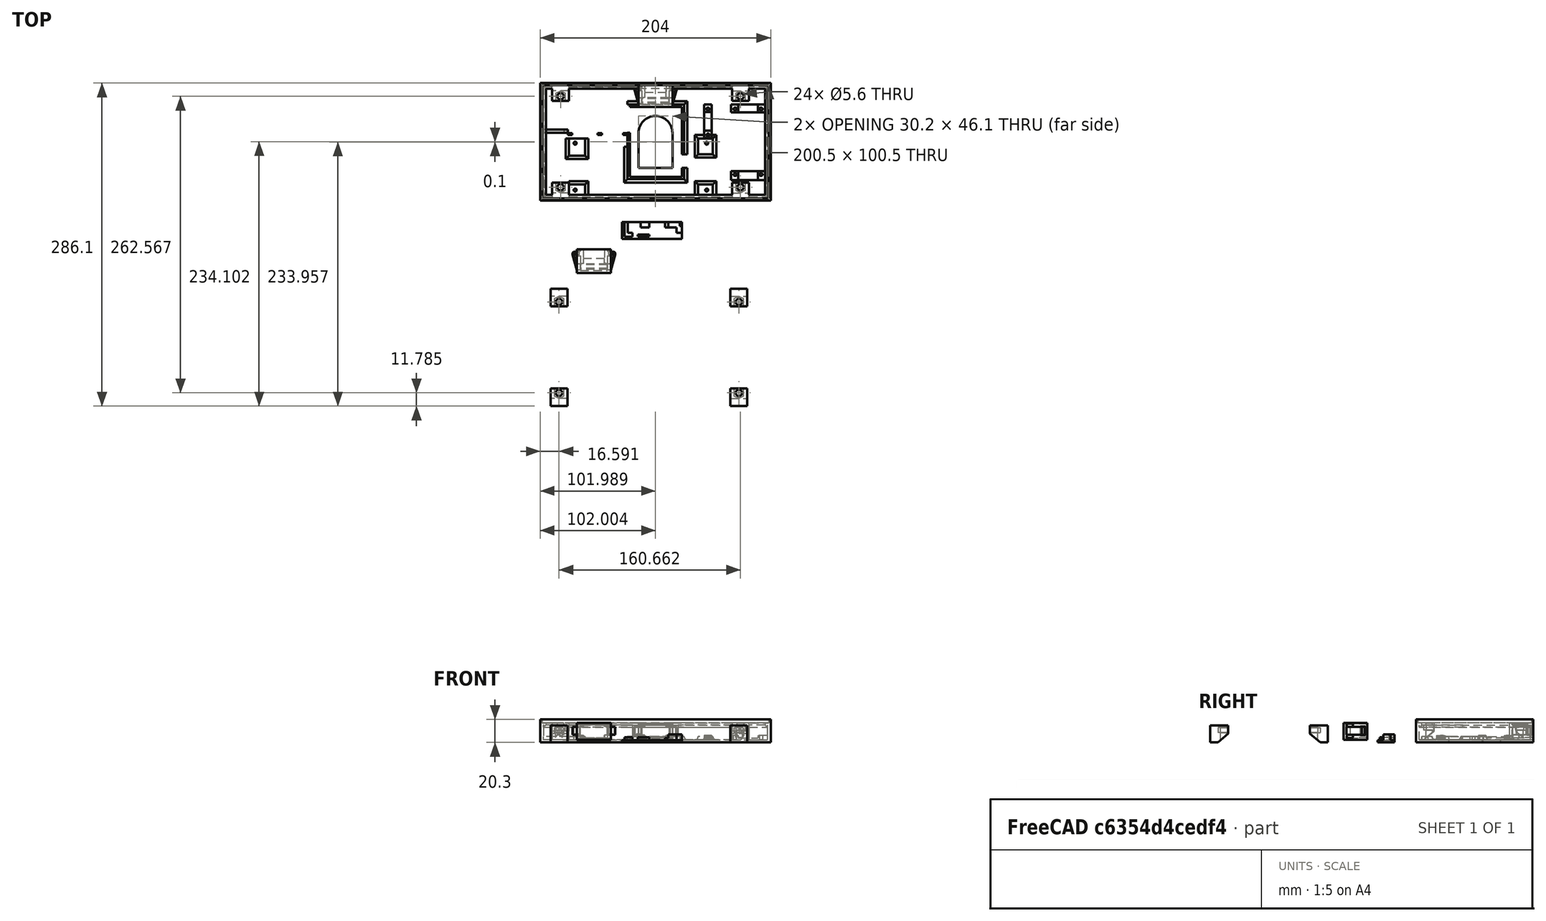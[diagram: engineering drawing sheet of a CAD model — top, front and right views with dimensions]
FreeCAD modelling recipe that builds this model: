
FCSTD DOCUMENT  (FreeCAD 0.18.4R)
Label: lamp.base.new
License: All rights reserved
LicenseURL: http://en.wikipedia.org/wiki/All_rights_reserved
objects: Part::Extrusion×98, Part::Feature×63, Part::Part2DObjectPython×54, Part::Cut×37, Part::MultiFuse×32, Part::MultiCommon×11, Part::Fuse×1
note: 296 computed .brp shape members not serialized (recipe doc carries the construction recipe); baked Part::Feature solids carry a one-line shape summary decoded from their .brp

FEATURE [Part::Feature] Fusion004001_solid  label="Power Connector Box-Hiddem"
  Placement = pos=(186.233,-140.75,0) rot=(0,0,1;0rad)
  shape: bbox 38 x 21 x 15 mm, 84 faces (baked)
FEATURE [Part::Feature] Fusion076089004005010001  label="RaspberryPi supplier"
  shape: bbox 32.15 x 67 x 4 mm, 24 faces, 2 solids (baked)
FEATURE [Part::Feature] Fusion076089004005008002002002002003004002009002004002005004002001  label="Power supply box cap - Hidden"
  shape: bbox 53 x 15.1 x 7 mm, 39 faces (baked)
FEATURE [Part::Part2DObjectPython] Rectangle007  # Draft 2D object (typed FeaturePython)
  ChamferSize = 0
  Columns = 1
  FilletRadius = 0
  Height = 1.8
  Length = 3.8
  MakeFace = true
  Placement = pos=(43.1036,-626.313,9.00025) rot=(1,0,0;3.14159rad)
  Rows = 1
FEATURE [Part::Part2DObjectPython] Rectangle008  # Draft 2D object (typed FeaturePython)
  ChamferSize = 0
  Columns = 1
  FilletRadius = 0
  Height = 1.8
  Length = 3.8
  MakeFace = true
  Placement = pos=(92.1036,-626.313,9.00025) rot=(1,0,0;3.14159rad)
  Rows = 1
FEATURE [Part::Part2DObjectPython] Rectangle009  # Draft 2D object (typed FeaturePython)
  ChamferSize = 0
  Columns = 1
  FilletRadius = 0
  Height = 1.8
  Length = 3.8
  MakeFace = true
  Placement = pos=(69.6036,-626.313,9.00025) rot=(1,0,0;3.14159rad)
  Rows = 1
FEATURE [Part::Extrusion] Extrusion037
  Base = -> Rectangle008
  Dir = (-1.26165e-08,1.08079e-10,-0.3)
  DirMode = 0
  FaceMakerClass = Part::FaceMakerBullseye
  LengthFwd = 0
  LengthRev = 0
  Solid = true
  Symmetric = false
FEATURE [Part::Extrusion] Extrusion038
  Base = -> Rectangle009
  Dir = (-1.26164e-08,1.08078e-10,-0.299999)
  DirMode = 0
  FaceMakerClass = Part::FaceMakerBullseye
  LengthFwd = 0
  LengthRev = 0
  Solid = true
  Symmetric = false
FEATURE [Part::Extrusion] Extrusion039
  Base = -> Rectangle007
  Dir = (-1.26164e-08,1.08078e-10,-0.299998)
  DirMode = 0
  FaceMakerClass = Part::FaceMakerBullseye
  LengthFwd = 0
  LengthRev = 0
  Solid = true
  Symmetric = false
FEATURE [Part::Part2DObjectPython] Rectangle010  # Draft 2D object (typed FeaturePython)
  ChamferSize = 0
  Columns = 1
  FilletRadius = 0
  Height = 3
  Length = 3
  MakeFace = true
  Placement = pos=(149.004,-645.218,12.0003) rot=(0,0.707107,-0.707107;3.14159rad)
  Rows = 1
FEATURE [Part::Part2DObjectPython] Circle002  # Draft 2D object (typed FeaturePython)
  FirstAngle = 0
  LastAngle = 0
  MakeFace = true
  Placement = pos=(149.004,-645.218,12.0003) rot=(0,0.707107,-0.707107;3.14159rad)
  Radius = 3
FEATURE [Part::Extrusion] Extrusion040
  Base = -> Rectangle010
  Dir = (-7e-16,47.0048,1.04e-14)
  DirMode = 0
  FaceMakerClass = Part::FaceMakerBullseye
  LengthFwd = 0
  LengthRev = 0
  Solid = true
  Symmetric = false
FEATURE [Part::Extrusion] Extrusion041
  Base = -> Circle002
  Dir = (-7e-16,47.0048,1.04e-14)
  DirMode = 0
  FaceMakerClass = Part::FaceMakerBullseye
  LengthFwd = 0
  LengthRev = 0
  Solid = true
  Symmetric = false
FEATURE [Part::Cut] Cut279012006003005
  Base = -> Extrusion040
  Tool = -> Extrusion041
FEATURE [Part::Part2DObjectPython] Rectangle011  # Draft 2D object (typed FeaturePython)
  ChamferSize = 0
  Columns = 1
  FilletRadius = 0
  Height = 3
  Length = 3
  MakeFace = true
  Placement = pos=(146.004,-667.213,9.00025) rot=(0.57735,-0.57735,-0.57735;2.0944rad)
  Rows = 1
FEATURE [Part::Part2DObjectPython] Circle003  # Draft 2D object (typed FeaturePython)
  FirstAngle = 0
  LastAngle = 0
  MakeFace = true
  Placement = pos=(146.004,-670.213,12.0003) rot=(0.57735,-0.57735,-0.57735;2.0944rad)
  Radius = 3
FEATURE [Part::Extrusion] Extrusion044
  Base = -> Rectangle011
  Dir = (-52.9386,1.18e-14,5.9e-15)
  DirMode = 0
  FaceMakerClass = Part::FaceMakerBullseye
  LengthFwd = 0
  LengthRev = 0
  Solid = true
  Symmetric = false
FEATURE [Part::Extrusion] Extrusion045
  Base = -> Circle003
  Dir = (-52.9386,1.18e-14,5.9e-15)
  DirMode = 0
  FaceMakerClass = Part::FaceMakerBullseye
  LengthFwd = 0
  LengthRev = 0
  Solid = true
  Symmetric = false
FEATURE [Part::Cut] Cut279012006003006
  Base = -> Extrusion044
  Tool = -> Extrusion045
FEATURE [Part::Feature] Face020
  shape: bbox 2e-07 x 3 x 3 mm, 1 faces, 0 solids (baked)
FEATURE [Part::Extrusion] Extrusion046
  Base = -> Face020
  Dir = (3,-7e-16,-3e-16)
  DirMode = 0
  FaceMakerClass = Part::FaceMakerBullseye
  LengthFwd = 0
  LengthRev = 0
  Solid = true
  Symmetric = false
FEATURE [Part::Part2DObjectPython] Circle004  # Draft 2D object (typed FeaturePython)
  FirstAngle = 0
  LastAngle = 0
  MakeFace = true
  Placement = pos=(149.004,-657.213,12.0003) rot=(-1,0,0;1.5708rad)
  Radius = 3
FEATURE [Part::Feature] Face021
  Placement = pos=(0,-11.9952,-3e-15) rot=(0,0,1;0rad)
  shape: bbox 3 x 2e-07 x 3 mm, 1 faces, 0 solids (baked)
FEATURE [Part::Extrusion] Extrusion047
  Base = -> Face021
  Dir = (2e-16,-13,-2.9e-15)
  DirMode = 0
  FaceMakerClass = Part::FaceMakerBullseye
  LengthFwd = 0
  LengthRev = 0
  Solid = true
  Symmetric = false
FEATURE [Part::Extrusion] Extrusion048
  Base = -> Circle004
  Dir = (-2e-16,-13,-2.9e-15)
  DirMode = 0
  FaceMakerClass = Part::FaceMakerBullseye
  LengthFwd = 0
  LengthRev = 0
  Solid = true
  Symmetric = false
FEATURE [Part::Cut] Cut279012006003007
  Base = -> Extrusion046
  Tool = -> Extrusion048
FEATURE [Part::Feature] Face023
  Placement = pos=(0,-24.9952,-6e-15) rot=(0,0,1;0rad)
  shape: bbox 3 x 2e-07 x 3 mm, 1 faces, 0 solids (baked)
FEATURE [Part::Extrusion] Extrusion051
  Base = -> Face023
  Dir = (0,3,7e-16)
  DirMode = 0
  FaceMakerClass = Part::FaceMakerBullseye
  LengthFwd = 0
  LengthRev = 0
  Solid = true
  Symmetric = false
FEATURE [Part::Cut] Cut279012006003008
  Base = -> Extrusion047
  Tool = -> Extrusion051
FEATURE [Part::MultiFuse] Fusion076089004005008002002002002003004002009002004002005004002002
  Shapes = -> [Cut279012006003006,Cut279012006003007,Cut279012006003008]
FEATURE [Part::MultiFuse] Fusion076089004005008002002002002003004002009002004002005004002003
  Shapes = -> [Cut279012006003005,Fusion076089004005008002002002002003004002009002004002005004002002]
FEATURE [Part::Feature] Face024
  shape: bbox 2e-07 x 3 x 3 mm, 1 faces, 0 solids (baked)
FEATURE [Part::Extrusion] Extrusion052
  Base = -> Face024
  Dir = (-0.0614462,0,0)
  DirMode = 0
  FaceMakerClass = Part::FaceMakerBullseye
  LengthFwd = 0
  LengthRev = 0
  Solid = true
  Symmetric = false
FEATURE [Part::MultiFuse] Fusion076089004005008002002002002003004002009002004002005004002004
  Shapes = -> [Fusion076089004005008002002002002003004002009002004002005004002003,Extrusion052]
FEATURE [Part::Part2DObjectPython] Rectangle012  # Draft 2D object (typed FeaturePython)
  ChamferSize = 0
  Columns = 1
  FilletRadius = 0
  Height = 3
  Length = 3
  MakeFace = true
  Placement = pos=(96.0036,-667.213,9.00025) rot=(0,0.707107,0.707107;3.14159rad)
  Rows = 1
  Support = -> [Fusion076089004005008002002002002003004002009002004002005004002004]
FEATURE [Part::Extrusion] Extrusion053
  Base = -> Rectangle012
  Dir = (6.9e-15,38.8,8.6e-15)
  DirMode = 0
  FaceMakerClass = Part::FaceMakerBullseye
  LengthFwd = 0
  LengthRev = 0
  Solid = true
  Symmetric = false
FEATURE [Part::Part2DObjectPython] Circle005  # Draft 2D object (typed FeaturePython)
  FirstAngle = 0
  LastAngle = 0
  MakeFace = true
  Placement = pos=(93.0036,-667.213,12.0003) rot=(0,0.707107,0.707107;3.14159rad)
  Radius = 3
  Support = -> [Extrusion053]
FEATURE [Part::Extrusion] Extrusion054
  Base = -> Circle005
  Dir = (6.9e-15,38.8,8.6e-15)
  DirMode = 0
  FaceMakerClass = Part::FaceMakerBullseye
  LengthFwd = 0
  LengthRev = 0
  Solid = true
  Symmetric = false
FEATURE [Part::Cut] Cut279012006003009
  Base = -> Extrusion053
  Tool = -> Extrusion054
FEATURE [Part::Feature] Face025
  shape: bbox 3 x 2e-07 x 3 mm, 1 faces, 0 solids (baked)
FEATURE [Part::Extrusion] Extrusion055
  Base = -> Face025
  Dir = (-5e-16,-2.96852,-7e-16)
  DirMode = 0
  FaceMakerClass = Part::FaceMakerBullseye
  LengthFwd = 0
  LengthRev = 0
  Solid = true
  Symmetric = false
FEATURE [Part::MultiFuse] Fusion076089004005008002002002002003004002009002004002005004002005
  Shapes = -> [Cut279012006003009,Extrusion055]
FEATURE [Part::Feature] Face026
  shape: bbox 3 x 2e-07 x 3 mm, 1 faces, 0 solids (baked)
FEATURE [Part::Extrusion] Extrusion056
  Base = -> Face026
  Dir = (-1.8e-15,-10,-2.2e-15)
  DirMode = 0
  FaceMakerClass = Part::FaceMakerBullseye
  LengthFwd = 0
  LengthRev = 0
  Solid = true
  Symmetric = false
FEATURE [Part::Cut] Cut279012006003010
  Base = -> Fusion076089004005008002002002002003004002009002004002005004002005
  Tool = -> Extrusion056
FEATURE [Part::Feature] Face028
  Placement = pos=(-1e-15,-2.96852,-1e-15) rot=(0,0,1;0rad)
  shape: bbox 3 x 2e-07 x 3 mm, 1 faces, 0 solids (baked)
FEATURE [Part::Extrusion] Extrusion057
  Base = -> Face028
  Dir = (5e-16,2.96852,7e-16)
  DirMode = 0
  FaceMakerClass = Part::FaceMakerBullseye
  LengthFwd = 0
  LengthRev = 0
  Solid = true
  Symmetric = false
FEATURE [Part::Feature] Face029
  Placement = pos=(-0.0614462,0,0) rot=(0,0,1;0rad)
  shape: bbox 2e-07 x 3 x 3 mm, 1 faces, 0 solids (baked)
FEATURE [Part::Extrusion] Extrusion058
  Base = -> Face029
  Dir = (3,-7e-16,-3e-16)
  DirMode = 0
  FaceMakerClass = Part::FaceMakerBullseye
  LengthFwd = 0
  LengthRev = 0
  Solid = true
  Symmetric = false
FEATURE [Part::Cut] Cut279012006003011
  Base = -> Cut279012006003010
  Tool = -> Extrusion057
FEATURE [Part::Cut] Cut279012006003012
  Base = -> Fusion076089004005008002002002002003004002009002004002005004002004
  Tool = -> Extrusion058
FEATURE [Part::Feature] Face030
  Placement = pos=(2.93855,-1e-15,0) rot=(0,0,1;0rad)
  shape: bbox 2e-07 x 3 x 3 mm, 1 faces, 0 solids (baked)
FEATURE [Part::Extrusion] Extrusion059
  Base = -> Face030
  Dir = (-3,7e-16,3e-16)
  DirMode = 0
  FaceMakerClass = Part::FaceMakerBullseye
  LengthFwd = 0
  LengthRev = 0
  Solid = true
  Symmetric = false
FEATURE [Part::Feature] Face031
  shape: bbox 3 x 2e-07 x 3 mm, 1 faces, 0 solids (baked)
FEATURE [Part::Extrusion] Extrusion060
  Base = -> Face031
  Dir = (-5e-16,-3,-7e-16)
  DirMode = 0
  FaceMakerClass = Part::FaceMakerBullseye
  LengthFwd = 0
  LengthRev = 0
  Solid = true
  Symmetric = false
FEATURE [Part::MultiCommon] Common
  Shapes = -> [Extrusion059,Extrusion060]
FEATURE [Part::MultiFuse] Fusion076089004005008002002002002003004002009002004002005004002006
  Shapes = -> [Common,Cut279012006003012,Cut279012006003011]
FEATURE [Part::Part2DObjectPython] Rectangle013  # Draft 2D object (typed FeaturePython)
  ChamferSize = 0
  Columns = 1
  FilletRadius = 0
  Height = 3
  Length = 3
  MakeFace = true
  Placement = pos=(146.004,-601.213,12.0003) rot=(0.57735,0.57735,-0.57735;4.18879rad)
  Rows = 1
  Support = -> [Fusion076089004005008002002002002003004002009002004002005004002006]
FEATURE [Part::Extrusion] Extrusion061
  Base = -> Rectangle013
  Dir = (-10.3,0,-2.3e-15)
  DirMode = 0
  FaceMakerClass = Part::FaceMakerBullseye
  LengthFwd = 0
  LengthRev = 0
  Solid = true
  Symmetric = false
FEATURE [Part::Part2DObjectPython] Circle006  # Draft 2D object (typed FeaturePython)
  FirstAngle = 0
  LastAngle = 0
  MakeFace = true
  Placement = pos=(146.004,-598.213,12.0003) rot=(0.57735,0.57735,-0.57735;4.18879rad)
  Radius = 3
FEATURE [Part::Extrusion] Extrusion062
  Base = -> Circle006
  Dir = (-10.3,0,-2.3e-15)
  DirMode = 0
  FaceMakerClass = Part::FaceMakerBullseye
  LengthFwd = 0
  LengthRev = 0
  Solid = true
  Symmetric = false
FEATURE [Part::Cut] Cut279012006003013
  Base = -> Extrusion061
  Tool = -> Extrusion062
FEATURE [Part::Feature] Face032
  shape: bbox 3 x 2e-07 x 3 mm, 1 faces, 0 solids (baked)
FEATURE [Part::Extrusion] Extrusion063
  Base = -> Face032
  Dir = (0,-3,-7e-16)
  DirMode = 0
  FaceMakerClass = Part::FaceMakerBullseye
  LengthFwd = 0
  LengthRev = 0
  Solid = true
  Symmetric = false
FEATURE [Part::Cut] Cut279012006003014
  Base = -> Fusion076089004005008002002002002003004002009002004002005004002006
  Tool = -> Extrusion063
FEATURE [Part::Feature] Face033
  Placement = pos=(0,-3,-1e-15) rot=(0,0,1;0rad)
  shape: bbox 3 x 2e-07 x 3 mm, 1 faces, 0 solids (baked)
FEATURE [Part::Extrusion] Extrusion064
  Base = -> Face033
  Dir = (0,3,7e-16)
  DirMode = 0
  FaceMakerClass = Part::FaceMakerBullseye
  LengthFwd = 0
  LengthRev = 0
  Solid = true
  Symmetric = false
FEATURE [Part::Feature] Face034
  shape: bbox 2e-07 x 3 x 3 mm, 1 faces, 0 solids (baked)
FEATURE [Part::Extrusion] Extrusion065
  Base = -> Face034
  Dir = (3,0,7e-16)
  DirMode = 0
  FaceMakerClass = Part::FaceMakerBullseye
  LengthFwd = 0
  LengthRev = 0
  Solid = true
  Symmetric = false
FEATURE [Part::MultiCommon] Common001
  Shapes = -> [Extrusion064,Extrusion065]
FEATURE [Part::MultiFuse] Fusion076089004005008002002002002003004002009002004002005004002007
  Shapes = -> [Common001,Cut279012006003013,Cut279012006003014]
FEATURE [Part::Part2DObjectPython] Rectangle014  # Draft 2D object (typed FeaturePython)
  ChamferSize = 0
  Columns = 1
  FilletRadius = 0
  Height = 3
  Length = 3
  MakeFace = true
  Placement = pos=(171.504,-671.954,9) rot=(0.57735,0.57735,0.57735;2.0944rad)
  Rows = 1
FEATURE [Part::Part2DObjectPython] Circle007  # Draft 2D object (typed FeaturePython)
  FirstAngle = 0
  LastAngle = 0
  MakeFace = true
  Placement = pos=(171.504,-668.954,12) rot=(0.57735,0.57735,0.57735;2.0944rad)
  Radius = 3
FEATURE [Part::Extrusion] Extrusion066
  Base = -> Rectangle014
  Dir = (-12.95,0,0)
  DirMode = 0
  FaceMakerClass = Part::FaceMakerBullseye
  LengthFwd = 0
  LengthRev = 0
  Solid = true
  Symmetric = false
FEATURE [Part::Extrusion] Extrusion067
  Base = -> Circle007
  Dir = (-12.95,0,0)
  DirMode = 0
  FaceMakerClass = Part::FaceMakerBullseye
  LengthFwd = 0
  LengthRev = 0
  Solid = true
  Symmetric = false
FEATURE [Part::Cut] Cut279012006003015
  Base = -> Extrusion066
  Tool = -> Extrusion067
FEATURE [Part::Part2DObjectPython] Rectangle015  # Draft 2D object (typed FeaturePython)
  ChamferSize = 0
  Columns = 1
  FilletRadius = 0
  Height = 3
  Length = 3
  MakeFace = true
  Placement = pos=(171.504,-631.118,9) rot=(0.57735,0.57735,0.57735;2.0944rad)
  Rows = 1
FEATURE [Part::Part2DObjectPython] Circle008  # Draft 2D object (typed FeaturePython)
  FirstAngle = 0
  LastAngle = 0
  MakeFace = true
  Placement = pos=(171.504,-628.118,12) rot=(0.57735,0.57735,0.57735;2.0944rad)
  Radius = 3
  Support = -> [Rectangle015]
FEATURE [Part::Extrusion] Extrusion068
  Base = -> Rectangle015
  Dir = (-12.95,0,0)
  DirMode = 0
  FaceMakerClass = Part::FaceMakerBullseye
  LengthFwd = 0
  LengthRev = 0
  Solid = true
  Symmetric = false
FEATURE [Part::Extrusion] Extrusion069
  Base = -> Circle008
  Dir = (-12.95,0,0)
  DirMode = 0
  FaceMakerClass = Part::FaceMakerBullseye
  LengthFwd = 0
  LengthRev = 0
  Solid = true
  Symmetric = false
FEATURE [Part::Cut] Cut279012006003016
  Base = -> Extrusion068
  Tool = -> Extrusion069
FEATURE [Part::Part2DObjectPython] Rectangle016  # Draft 2D object (typed FeaturePython)
  ChamferSize = 0
  Columns = 1
  FilletRadius = 0
  Height = 2.86268
  Length = 2.86268
  MakeFace = true
  Placement = pos=(58.2286,-671.954,9.13732) rot=(0.57735,0.57735,0.57735;2.0944rad)
  Rows = 1
FEATURE [Part::Extrusion] Extrusion070
  Base = -> Rectangle016
  Dir = (-14.025,7.8e-15,7e-15)
  DirMode = 0
  FaceMakerClass = Part::FaceMakerBullseye
  LengthFwd = 0
  LengthRev = 0
  Solid = true
  Symmetric = false
FEATURE [Part::Part2DObjectPython] Circle009  # Draft 2D object (typed FeaturePython)
  FirstAngle = 0
  LastAngle = 0
  MakeFace = true
  Placement = pos=(58.2286,-669.091,12) rot=(0.57735,0.57735,0.57735;2.0944rad)
  Radius = 2.86268
FEATURE [Part::Extrusion] Extrusion071
  Base = -> Circle009
  Dir = (-14.025,7.8e-15,7e-15)
  DirMode = 0
  FaceMakerClass = Part::FaceMakerBullseye
  LengthFwd = 0
  LengthRev = 0
  Solid = true
  Symmetric = false
FEATURE [Part::Cut] Cut279012006003017
  Base = -> Extrusion070
  Tool = -> Extrusion071
FEATURE [Part::Part2DObjectPython] Rectangle017  # Draft 2D object (typed FeaturePython)
  ChamferSize = 0
  Columns = 1
  FilletRadius = 0
  Height = 3
  Length = 3
  MakeFace = true
  Placement = pos=(58.2286,-649.418,9) rot=(0.57735,0.57735,0.57735;2.0944rad)
  Rows = 1
FEATURE [Part::Part2DObjectPython] Circle010  # Draft 2D object (typed FeaturePython)
  FirstAngle = 0
  LastAngle = 0
  MakeFace = true
  Placement = pos=(58.2286,-649.418,12) rot=(0.57735,0.57735,0.57735;2.0944rad)
  Radius = 3
FEATURE [Part::Extrusion] Extrusion072
  Base = -> Rectangle017
  Dir = (-14.025,7.8e-15,7e-15)
  DirMode = 0
  FaceMakerClass = Part::FaceMakerBullseye
  LengthFwd = 0
  LengthRev = 0
  Solid = true
  Symmetric = false
FEATURE [Part::Extrusion] Extrusion073
  Base = -> Circle010
  Dir = (-14.025,7.8e-15,7e-15)
  DirMode = 0
  FaceMakerClass = Part::FaceMakerBullseye
  LengthFwd = 0
  LengthRev = 0
  Solid = true
  Symmetric = false
FEATURE [Part::Cut] Cut279012006003018
  Base = -> Extrusion072
  Tool = -> Extrusion073
FEATURE [Part::Part2DObjectPython] Rectangle018  # Draft 2D object (typed FeaturePython)
  ChamferSize = 0
  Columns = 1
  FilletRadius = 0
  Height = 3
  Length = 3
  MakeFace = true
  Placement = pos=(174.504,-671.954,9) rot=(0,0.707107,0.707107;3.14159rad)
  Rows = 1
FEATURE [Part::Part2DObjectPython] Circle011  # Draft 2D object (typed FeaturePython)
  FirstAngle = 0
  LastAngle = 0
  MakeFace = true
  Placement = pos=(174.504,-671.954,12) rot=(0,0.707107,0.707107;3.14159rad)
  Radius = 3
FEATURE [Part::Extrusion] Extrusion074
  Base = -> Rectangle018
  Dir = (1.3e-15,-9.16419,2e-15)
  DirMode = 0
  FaceMakerClass = Part::FaceMakerBullseye
  LengthFwd = 0
  LengthRev = 0
  Solid = true
  Symmetric = false
FEATURE [Part::Extrusion] Extrusion075
  Base = -> Circle011
  Dir = (1.3e-15,-9.16419,2e-15)
  DirMode = 0
  FaceMakerClass = Part::FaceMakerBullseye
  LengthFwd = 0
  LengthRev = 0
  Solid = true
  Symmetric = false
FEATURE [Part::Cut] Cut279012006003019
  Base = -> Extrusion074
  Tool = -> Extrusion075
FEATURE [Part::Part2DObjectPython] Rectangle019  # Draft 2D object (typed FeaturePython)
  ChamferSize = 0
  Columns = 1
  FilletRadius = 0
  Height = 3
  Length = 3
  MakeFace = true
  Placement = pos=(158.554,-671.954,9) rot=(0,0.707107,0.707107;3.14159rad)
  Rows = 1
FEATURE [Part::Part2DObjectPython] Circle012  # Draft 2D object (typed FeaturePython)
  FirstAngle = 0
  LastAngle = 0
  MakeFace = true
  Placement = pos=(155.554,-671.954,12) rot=(0,0.707107,0.707107;3.14159rad)
  Radius = 3
  Support = -> [Rectangle019]
FEATURE [Part::Extrusion] Extrusion076
  Base = -> Rectangle019
  Dir = (1.3e-15,-9.16419,2e-15)
  DirMode = 0
  FaceMakerClass = Part::FaceMakerBullseye
  LengthFwd = 0
  LengthRev = 0
  Solid = true
  Symmetric = false
FEATURE [Part::Extrusion] Extrusion077
  Base = -> Circle012
  Dir = (1.3e-15,-9.16419,2e-15)
  DirMode = 0
  FaceMakerClass = Part::FaceMakerBullseye
  LengthFwd = 0
  LengthRev = 0
  Solid = true
  Symmetric = false
FEATURE [Part::Cut] Cut279012006003020
  Base = -> Extrusion076
  Tool = -> Extrusion077
FEATURE [Part::Part2DObjectPython] Rectangle020  # Draft 2D object (typed FeaturePython)
  ChamferSize = 0
  Columns = 1
  FilletRadius = 0
  Height = 2.86268
  Length = 3
  MakeFace = true
  Placement = pos=(61.2286,-671.954,9.13732) rot=(0,0.707107,0.707107;3.14159rad)
  Rows = 1
FEATURE [Part::Part2DObjectPython] Circle013  # Draft 2D object (typed FeaturePython)
  FirstAngle = 0
  LastAngle = 0
  MakeFace = true
  Placement = pos=(61.2286,-671.954,12) rot=(0,0.707107,0.707107;3.14159rad)
  Radius = 2.86268
FEATURE [Part::Extrusion] Extrusion078
  Base = -> Rectangle020
  Dir = (1.3e-15,-9.16419,2e-15)
  DirMode = 0
  FaceMakerClass = Part::FaceMakerBullseye
  LengthFwd = 0
  LengthRev = 0
  Solid = true
  Symmetric = false
FEATURE [Part::Extrusion] Extrusion079
  Base = -> Circle013
  Dir = (1.3e-15,-9.16419,2e-15)
  DirMode = 0
  FaceMakerClass = Part::FaceMakerBullseye
  LengthFwd = 0
  LengthRev = 0
  Solid = true
  Symmetric = false
FEATURE [Part::Cut] Cut279012006003021
  Base = -> Extrusion078
  Tool = -> Extrusion079
FEATURE [Part::Part2DObjectPython] Rectangle021  # Draft 2D object (typed FeaturePython)
  ChamferSize = 0
  Columns = 1
  FilletRadius = 0
  Height = 3
  Length = 3
  MakeFace = true
  Placement = pos=(158.554,-645.218,12) rot=(0,0.707107,-0.707107;3.14159rad)
  Rows = 1
FEATURE [Part::Part2DObjectPython] Circle014  # Draft 2D object (typed FeaturePython)
  FirstAngle = 0
  LastAngle = 0
  MakeFace = true
  Placement = pos=(155.554,-645.218,12) rot=(0,0.707107,-0.707107;3.14159rad)
  Radius = 3
FEATURE [Part::Extrusion] Extrusion080
  Base = -> Rectangle021
  Dir = (-6.4e-15,14.1,1.847e-13)
  DirMode = 0
  FaceMakerClass = Part::FaceMakerBullseye
  LengthFwd = 0
  LengthRev = 0
  Solid = true
  Symmetric = false
FEATURE [Part::Extrusion] Extrusion081
  Base = -> Circle014
  Dir = (-6.4e-15,14.1,1.847e-13)
  DirMode = 0
  FaceMakerClass = Part::FaceMakerBullseye
  LengthFwd = 0
  LengthRev = 0
  Solid = true
  Symmetric = false
FEATURE [Part::Cut] Cut279012006003022
  Base = -> Extrusion080
  Tool = -> Extrusion081
FEATURE [Part::Part2DObjectPython] Rectangle022  # Draft 2D object (typed FeaturePython)
  ChamferSize = 0
  Columns = 1
  FilletRadius = 0
  Height = 3
  Length = 3
  MakeFace = true
  Placement = pos=(174.504,-645.218,12) rot=(0,0.707107,-0.707107;3.14159rad)
  Rows = 1
FEATURE [Part::Part2DObjectPython] Circle015  # Draft 2D object (typed FeaturePython)
  FirstAngle = 0
  LastAngle = 0
  MakeFace = true
  Placement = pos=(174.504,-645.218,12) rot=(0,0.707107,-0.707107;3.14159rad)
  Radius = 3
FEATURE [Part::Extrusion] Extrusion082
  Base = -> Rectangle022
  Dir = (-6.4e-15,14.1,1.847e-13)
  DirMode = 0
  FaceMakerClass = Part::FaceMakerBullseye
  LengthFwd = 0
  LengthRev = 0
  Solid = true
  Symmetric = false
FEATURE [Part::Extrusion] Extrusion083
  Base = -> Circle015
  Dir = (-6.4e-15,14.1,1.847e-13)
  DirMode = 0
  FaceMakerClass = Part::FaceMakerBullseye
  LengthFwd = 0
  LengthRev = 0
  Solid = true
  Symmetric = false
FEATURE [Part::Cut] Cut279012006003023
  Base = -> Extrusion082
  Tool = -> Extrusion083
FEATURE [Part::Part2DObjectPython] Rectangle023  # Draft 2D object (typed FeaturePython)
  ChamferSize = 0
  Columns = 1
  FilletRadius = 0
  Height = 3
  Length = 3
  MakeFace = true
  Placement = pos=(44.2036,-631.118,9) rot=(0,0.707107,0.707107;3.14159rad)
  Rows = 1
FEATURE [Part::Part2DObjectPython] Circle016  # Draft 2D object (typed FeaturePython)
  FirstAngle = 0
  LastAngle = 0
  MakeFace = true
  Placement = pos=(41.2036,-631.118,12) rot=(0,0.707107,0.707107;3.14159rad)
  Radius = 3
  Support = -> [Rectangle023]
FEATURE [Part::Extrusion] Extrusion084
  Base = -> Rectangle023
  Dir = (0,-15.3,3.4e-15)
  DirMode = 0
  FaceMakerClass = Part::FaceMakerBullseye
  LengthFwd = 0
  LengthRev = 0
  Solid = true
  Symmetric = false
FEATURE [Part::Extrusion] Extrusion085
  Base = -> Circle016
  Dir = (0,-15.3,3.4e-15)
  DirMode = 0
  FaceMakerClass = Part::FaceMakerBullseye
  LengthFwd = 0
  LengthRev = 0
  Solid = true
  Symmetric = false
FEATURE [Part::Cut] Cut279012006003024
  Base = -> Extrusion084
  Tool = -> Extrusion085
FEATURE [Part::Part2DObjectPython] Rectangle024  # Draft 2D object (typed FeaturePython)
  ChamferSize = 0
  Columns = 1
  FilletRadius = 0
  Height = 3
  Length = 3
  MakeFace = true
  Placement = pos=(61.2286,-631.118,9) rot=(0,0.707107,0.707107;3.14159rad)
  Rows = 1
FEATURE [Part::Part2DObjectPython] Circle017  # Draft 2D object (typed FeaturePython)
  FirstAngle = 0
  LastAngle = 0
  MakeFace = true
  Placement = pos=(61.2286,-631.118,12) rot=(0,0.707107,0.707107;3.14159rad)
  Radius = 3
  Support = -> [Rectangle024]
FEATURE [Part::Extrusion] Extrusion086
  Base = -> Rectangle024
  Dir = (0,-15.3,3.4e-15)
  DirMode = 0
  FaceMakerClass = Part::FaceMakerBullseye
  LengthFwd = 0
  LengthRev = 0
  Solid = true
  Symmetric = false
FEATURE [Part::Extrusion] Extrusion087
  Base = -> Circle017
  Dir = (0,-15.3,3.4e-15)
  DirMode = 0
  FaceMakerClass = Part::FaceMakerBullseye
  LengthFwd = 0
  LengthRev = 0
  Solid = true
  Symmetric = false
FEATURE [Part::Cut] Cut279012006003025
  Base = -> Extrusion086
  Tool = -> Extrusion087
FEATURE [Part::Part2DObjectPython] Rectangle025  # Draft 2D object (typed FeaturePython)
  ChamferSize = 0
  Columns = 1
  FilletRadius = 0
  Height = 3
  Length = 3
  MakeFace = true
  Placement = pos=(171.504,-645.218,12) rot=(0.57735,-0.57735,0.57735;4.18879rad)
  Rows = 1
FEATURE [Part::Part2DObjectPython] Circle018  # Draft 2D object (typed FeaturePython)
  FirstAngle = 0
  LastAngle = 0
  MakeFace = true
  Placement = pos=(171.504,-648.218,12) rot=(0.57735,-0.57735,0.57735;4.18879rad)
  Radius = 3
FEATURE [Part::Extrusion] Extrusion088
  Base = -> Rectangle025
  Dir = (-12.95,-5.8e-15,5.8e-15)
  DirMode = 0
  FaceMakerClass = Part::FaceMakerBullseye
  LengthFwd = 0
  LengthRev = 0
  Solid = true
  Symmetric = false
FEATURE [Part::Extrusion] Extrusion089
  Base = -> Circle018
  Dir = (-12.95,-5.8e-15,5.8e-15)
  DirMode = 0
  FaceMakerClass = Part::FaceMakerBullseye
  LengthFwd = 0
  LengthRev = 0
  Solid = true
  Symmetric = false
FEATURE [Part::Cut] Cut279012006003026
  Base = -> Extrusion088
  Tool = -> Extrusion089
FEATURE [Part::Feature] Face035
  shape: bbox 2e-07 x 3 x 3 mm, 1 faces, 0 solids (baked)
FEATURE [Part::Extrusion] Extrusion090
  Base = -> Face035
  Dir = (3,0,0)
  DirMode = 0
  FaceMakerClass = Part::FaceMakerBullseye
  LengthFwd = 0
  LengthRev = 0
  Solid = true
  Symmetric = false
FEATURE [Part::Feature] Face036
  shape: bbox 3 x 2e-07 x 3 mm, 1 faces, 0 solids (baked)
FEATURE [Part::Extrusion] Extrusion091
  Base = -> Face036
  Dir = (-1.4e-15,2.99725,3.93e-14)
  DirMode = 0
  FaceMakerClass = Part::FaceMakerBullseye
  LengthFwd = 0
  LengthRev = 0
  Solid = true
  Symmetric = false
FEATURE [Part::MultiCommon] Common002
  Shapes = -> [Extrusion090,Extrusion091]
FEATURE [Part::Feature] Face037
  shape: bbox 2e-07 x 3 x 3 mm, 1 faces, 0 solids (baked)
FEATURE [Part::Extrusion] Extrusion092
  Base = -> Face037
  Dir = (3,1.3e-15,-1.3e-15)
  DirMode = 0
  FaceMakerClass = Part::FaceMakerBullseye
  LengthFwd = 0
  LengthRev = 0
  Solid = true
  Symmetric = false
FEATURE [Part::Feature] Face038
  shape: bbox 3 x 2e-07 x 3 mm, 1 faces, 0 solids (baked)
FEATURE [Part::Extrusion] Extrusion093
  Base = -> Face038
  Dir = (1.4e-15,-3,-3.93e-14)
  DirMode = 0
  FaceMakerClass = Part::FaceMakerBullseye
  LengthFwd = 0
  LengthRev = 0
  Solid = true
  Symmetric = false
FEATURE [Part::MultiCommon] Common003
  Shapes = -> [Extrusion093,Extrusion092]
FEATURE [Part::Feature] Face039
  shape: bbox 3 x 2e-07 x 3 mm, 1 faces, 0 solids (baked)
FEATURE [Part::Extrusion] Extrusion094
  Base = -> Face039
  Dir = (1.4e-15,-3,-3.93e-14)
  DirMode = 0
  FaceMakerClass = Part::FaceMakerBullseye
  LengthFwd = 0
  LengthRev = 0
  Solid = true
  Symmetric = false
FEATURE [Part::Feature] Face040
  shape: bbox 2e-07 x 3 x 3 mm, 1 faces, 0 solids (baked)
FEATURE [Part::Extrusion] Extrusion095
  Base = -> Face040
  Dir = (-3,-1.3e-15,1.3e-15)
  DirMode = 0
  FaceMakerClass = Part::FaceMakerBullseye
  LengthFwd = 0
  LengthRev = 0
  Solid = true
  Symmetric = false
FEATURE [Part::MultiCommon] Common004
  Shapes = -> [Extrusion095,Extrusion094]
FEATURE [Part::Feature] Face041
  shape: bbox 3 x 2e-07 x 3 mm, 1 faces, 0 solids (baked)
FEATURE [Part::Extrusion] Extrusion096
  Base = -> Face041
  Dir = (-1.4e-15,3,3.93e-14)
  DirMode = 0
  FaceMakerClass = Part::FaceMakerBullseye
  LengthFwd = 0
  LengthRev = 0
  Solid = true
  Symmetric = false
FEATURE [Part::Feature] Face042
  shape: bbox 2e-07 x 3 x 3 mm, 1 faces, 0 solids (baked)
FEATURE [Part::Extrusion] Extrusion097
  Base = -> Face042
  Dir = (-3,0,0)
  DirMode = 0
  FaceMakerClass = Part::FaceMakerBullseye
  LengthFwd = 0
  LengthRev = 0
  Solid = true
  Symmetric = false
FEATURE [Part::MultiCommon] Common005
  Shapes = -> [Extrusion096,Extrusion097]
FEATURE [Part::MultiFuse] Fusion076089004005008002002002002003004002009002004002005004002008
  Shapes = -> [Cut279012006003016,Common005,Common002,Cut279012006003022,Common004,Cut279012006003023,Common003,Cut279012006003026]
FEATURE [Part::Feature] Face043
  shape: bbox 3 x 2e-07 x 3 mm, 1 faces, 0 solids (baked)
FEATURE [Part::Extrusion] Extrusion098
  Base = -> Face043
  Dir = (-4e-16,3,-7e-16)
  DirMode = 0
  FaceMakerClass = Part::FaceMakerBullseye
  LengthFwd = 0
  LengthRev = 0
  Solid = true
  Symmetric = false
FEATURE [Part::Feature] Face044
  shape: bbox 2e-07 x 3 x 3 mm, 1 faces, 0 solids (baked)
FEATURE [Part::Extrusion] Extrusion099
  Base = -> Face044
  Dir = (-3,0,0)
  DirMode = 0
  FaceMakerClass = Part::FaceMakerBullseye
  LengthFwd = 0
  LengthRev = 0
  Solid = true
  Symmetric = false
FEATURE [Part::MultiCommon] Common006
  Shapes = -> [Extrusion099,Extrusion098]
FEATURE [Part::MultiFuse] Fusion076089004005008002002002002003004002009002004002005004002010
  Shapes = -> [Cut279012006003020,Cut279012006003015,Common006]
FEATURE [Part::Feature] Face045
  shape: bbox 3 x 2e-07 x 3 mm, 1 faces, 0 solids (baked)
FEATURE [Part::Extrusion] Extrusion100
  Base = -> Face045
  Dir = (-4e-16,3,-7e-16)
  DirMode = 0
  FaceMakerClass = Part::FaceMakerBullseye
  LengthFwd = 0
  LengthRev = 0
  Solid = true
  Symmetric = false
FEATURE [Part::Feature] Face046
  shape: bbox 2e-07 x 3 x 3 mm, 1 faces, 0 solids (baked)
FEATURE [Part::Extrusion] Extrusion101
  Base = -> Face046
  Dir = (3,0,0)
  DirMode = 0
  FaceMakerClass = Part::FaceMakerBullseye
  LengthFwd = 0
  LengthRev = 0
  Solid = true
  Symmetric = false
FEATURE [Part::MultiCommon] Common007
  Shapes = -> [Extrusion101,Extrusion100]
FEATURE [Part::MultiFuse] Fusion076089004005008002002002002003004002009002004002005004002011
  Shapes = -> [Fusion076089004005008002002002002003004002009002004002005004002010,Common007,Cut279012006003019]
FEATURE [Part::Feature] Face047
  shape: bbox 3 x 2e-07 x 2.863 mm, 1 faces, 0 solids (baked)
FEATURE [Part::Extrusion] Extrusion102
  Base = -> Face047
  Dir = (-4e-16,2.86268,-6e-16)
  DirMode = 0
  FaceMakerClass = Part::FaceMakerBullseye
  LengthFwd = 0
  LengthRev = 0
  Solid = true
  Symmetric = false
FEATURE [Part::Feature] Face048
  shape: bbox 2e-07 x 2.863 x 2.863 mm, 1 faces, 0 solids (baked)
FEATURE [Part::Extrusion] Extrusion103
  Base = -> Face048
  Dir = (3,-1.7e-15,-1.5e-15)
  DirMode = 0
  FaceMakerClass = Part::FaceMakerBullseye
  LengthFwd = 0
  LengthRev = 0
  Solid = true
  Symmetric = false
FEATURE [Part::MultiCommon] Common008
  Shapes = -> [Extrusion103,Extrusion102]
FEATURE [Part::MultiFuse] Fusion076089004005008002002002002003004002009002004002005004002013
  Shapes = -> [Cut279012006003017,Common008,Cut279012006003021]
FEATURE [Part::Feature] Face049
  shape: bbox 3 x 2e-07 x 3 mm, 1 faces, 0 solids (baked)
FEATURE [Part::Extrusion] Extrusion104
  Base = -> Face049
  Dir = (0,-3,7e-16)
  DirMode = 0
  FaceMakerClass = Part::FaceMakerBullseye
  LengthFwd = 0
  LengthRev = 0
  Solid = true
  Symmetric = false
FEATURE [Part::Feature] Face050
  shape: bbox 2e-07 x 3 x 3 mm, 1 faces, 0 solids (baked)
FEATURE [Part::Extrusion] Extrusion105
  Base = -> Face050
  Dir = (3,-1.7e-15,-1.5e-15)
  DirMode = 0
  FaceMakerClass = Part::FaceMakerBullseye
  LengthFwd = 0
  LengthRev = 0
  Solid = true
  Symmetric = false
FEATURE [Part::MultiCommon] Common009
  Shapes = -> [Extrusion105,Extrusion104]
FEATURE [Part::Feature] Face051
  shape: bbox 3 x 2e-07 x 3 mm, 1 faces, 0 solids (baked)
FEATURE [Part::Extrusion] Extrusion106
  Base = -> Face051
  Dir = (0,-3,7e-16)
  DirMode = 0
  FaceMakerClass = Part::FaceMakerBullseye
  LengthFwd = 0
  LengthRev = 0
  Solid = true
  Symmetric = false
FEATURE [Part::Feature] Face052
  shape: bbox 2e-07 x 3 x 3 mm, 1 faces, 0 solids (baked)
FEATURE [Part::Extrusion] Extrusion107
  Base = -> Face052
  Dir = (-3,1.7e-15,1.5e-15)
  DirMode = 0
  FaceMakerClass = Part::FaceMakerBullseye
  LengthFwd = 0
  LengthRev = 0
  Solid = true
  Symmetric = false
FEATURE [Part::MultiCommon] Common010
  Shapes = -> [Extrusion107,Extrusion106]
FEATURE [Part::MultiFuse] Fusion076089004005008002002002002003004002009002004002005004002015
  Shapes = -> [Cut279012006003024,Common010,Cut279012006003018,Common009,Cut279012006003025]
FEATURE [Part::Feature] Cut279001  label="Cut280"
  Placement = pos=(255.302,-5.37176,8.7e-14) rot=(0,0,1;0rad)
  shape: bbox 127.3 x 50 x 3 mm, 28 faces, 4 solids (baked)
FEATURE [Part::MultiFuse] Fusion  label="Transformator supplier"
  Shapes = -> [Cut279001,Fusion076089004005008002002002002003004002009002004002005004002008,Fusion076089004005008002002002002003004002009002004002005004002011,Fusion076089004005008002002002002003004002009002004002005004002013,Fusion076089004005008002002002002003004002009002004002005004002015]
FEATURE [Part::Feature] Fusion076089004005008002002002002003004002001  label="Fusion076089004005008002002002002003004003"
  shape: bbox 204 x 104 x 20.3 mm, 70 faces, 2 solids (baked)
FEATURE [Part::MultiFuse] Fusion076089004005008002002002002003004002009002004002005004002016
  Shapes = -> [Extrusion038,Extrusion039,Extrusion037]
FEATURE [Part::Cut] Cut
  Base = -> Fusion076089004005008002002002002003004002001
  Tool = -> Fusion076089004005008002002002002003004002009002004002005004002016
FEATURE [Part::MultiFuse] Fusion076089004005008002002002002003004002009002004002005004002017  label="Frame"
  Shapes = -> [Fusion076089004005008002002002002003004002009002004002005004002007,Cut]
FEATURE [Part::MultiFuse] Fusion076089004005008002002002002003004002009002004002005004002022  label="Suppliers-Original"
  Shapes = -> [Fusion076089004005010001,Fusion]
FEATURE [Part::Part2DObjectPython] Rectangle  # Draft 2D object (typed FeaturePython)
  ChamferSize = 0
  Columns = 1
  FilletRadius = 0
  Height = 31.1
  Length = 30.2
  MakeFace = true
  Placement = pos=(105.589,-657.313,9.00034) rot=(-1,0,0;2.2e-05rad)
  Rows = 1
FEATURE [Part::Part2DObjectPython] Circle019  # Draft 2D object (typed FeaturePython)
  FirstAngle = 0
  LastAngle = 0
  MakeFace = true
  Placement = pos=(120.689,-626.213,8.99966) rot=(0,0,1;0rad)
  Radius = 15.1
FEATURE [Part::Extrusion] Extrusion
  Base = -> Rectangle
  Dir = (0,-5.04303e-05,-2.29983)
  DirMode = 0
  FaceMakerClass = Part::FaceMakerBullseye
  LengthFwd = 0
  LengthRev = 0
  Solid = true
  Symmetric = false
FEATURE [Part::Extrusion] Extrusion108
  Base = -> Circle019
  Dir = (0,0,-2.29966)
  DirMode = 0
  FaceMakerClass = Part::FaceMakerBullseye
  LengthFwd = 0
  LengthRev = 0
  Solid = true
  Symmetric = false
FEATURE [Part::MultiFuse] Fusion076089004005008002002002002003004002009002004002005004002026
  Shapes = -> [Extrusion,Extrusion108]
FEATURE [Part::Cut] Cut279012006003027  label="FRAME with bigger hole-I do not know why it is here"
  Base = -> Fusion076089004005008002002002002003004002009002004002005004002017
  Tool = -> Fusion076089004005008002002002002003004002009002004002005004002026
FEATURE [Part::Cut] Cut279012006003028  label="FRAME with bigger hole001"
  Base = -> Fusion076089004005008002002002002003004002009002004002005004002017
  Tool = -> Fusion076089004005008002002002002003004002009002004002005004002026
FEATURE [Part::Feature] Fusion_rev_child2_child0_solid001  label="Fusion (Rev).2.0 (Solid)001"
  shape: bbox 15 x 15.78 x 15 mm, 15 faces (baked)
FEATURE [Part::Feature] Fusion_rev_child3_child0_solid001  label="Fusion (Rev).3.0 (Solid)001"
  shape: bbox 15 x 15.75 x 15 mm, 15 faces (baked)
FEATURE [Part::Feature] Fusion_rev_child1_child0_solid001  label="Fusion (Rev).1.0 (Solid)001"
  shape: bbox 15 x 15.75 x 15 mm, 15 faces (baked)
FEATURE [Part::Feature] Fusion_rev_child0_child0_solid001  label="Fusion (Rev).0.0 (Solid)001"
  shape: bbox 15 x 15.78 x 15 mm, 15 faces (baked)
FEATURE [Part::MultiFuse] Fusion076089004005008002002002002003004002009002004002005004002027  label="FRAME with screws"
  Shapes = -> [Fusion_rev_child2_child0_solid001,Fusion_rev_child3_child0_solid001,Fusion_rev_child1_child0_solid001,Fusion_rev_child0_child0_solid001,Cut279012006003028]
FEATURE [Part::Feature] Fusion_rev_child0_child0_solid  label="Screw hole 1 - hidden"
  Placement = pos=(-1.4124,-182.098,-2.3) rot=(0,0,1;0rad)
  shape: bbox 15 x 15.78 x 15 mm, 15 faces (baked)
FEATURE [Part::Feature] Fusion_rev_child2_child0_solid  label="Screw hole 2 - hidden"
  Placement = pos=(-1.4124,-182.098,-2.3) rot=(0,0,1;0rad)
  shape: bbox 15 x 15.78 x 15 mm, 15 faces (baked)
FEATURE [Part::Feature] Fusion_rev_child3_child0_solid  label="Screw hole 3 - hidden"
  Placement = pos=(-1.4124,-182.098,-2.3) rot=(0,0,1;0rad)
  shape: bbox 15 x 15.75 x 15 mm, 15 faces (baked)
FEATURE [Part::Feature] Fusion_rev_child1_child0_solid  label="Screw hole 4 - hidden"
  Placement = pos=(-1.4124,-182.098,-2.3) rot=(0,0,1;0rad)
  shape: bbox 15 x 15.75 x 15 mm, 15 faces (baked)
FEATURE [Part::Feature] Face058
  shape: bbox 7.839e-07 x 3 x 15 mm, 1 faces, 0 solids (baked)
FEATURE [Part::Extrusion] Extrusion119
  Base = -> Face058
  Dir = (-5,0,0)
  DirMode = 0
  FaceMakerClass = Part::FaceMakerBullseye
  LengthFwd = 0
  LengthRev = 0
  Solid = true
  Symmetric = false
FEATURE [Part::Feature] Face059
  shape: bbox 7.839e-07 x 3 x 15 mm, 1 faces, 0 solids (baked)
FEATURE [Part::Extrusion] Extrusion120
  Base = -> Face059
  Dir = (5,0,0)
  DirMode = 0
  FaceMakerClass = Part::FaceMakerBullseye
  LengthFwd = 0
  LengthRev = 0
  Solid = true
  Symmetric = false
FEATURE [Part::Part2DObjectPython] Rectangle030  # Draft 2D object (typed FeaturePython)
  ChamferSize = 0
  Columns = 1
  FilletRadius = 0
  Height = 4.25
  Length = 5
  MakeFace = true
  Placement = pos=(140.704,-584.118,9) rot=(0,0.707107,0.707107;3.14159rad)
  Rows = 1
  Support = -> [Extrusion119]
FEATURE [Part::Extrusion] Extrusion121
  Base = -> Rectangle030
  Dir = (0,-1,2e-16)
  DirMode = 0
  FaceMakerClass = Part::FaceMakerBullseye
  LengthFwd = 0
  LengthRev = 0
  Solid = true
  Symmetric = false
FEATURE [Part::MultiFuse] Fusion076089004005008002002002002003004002009002004002005004002028003
  Shapes = -> [Extrusion119,Extrusion121]
FEATURE [Part::Feature] Face060
  shape: bbox 5 x 1 x 7.839e-07 mm, 1 faces, 0 solids (baked)
FEATURE [Part::Extrusion] Extrusion122
  Base = -> Face060
  Dir = (0,-3e-16,-1.25)
  DirMode = 0
  FaceMakerClass = Part::FaceMakerBullseye
  LengthFwd = 0
  LengthRev = 0
  Solid = true
  Symmetric = false
FEATURE [Part::Cut] Cut279012006003037
  Base = -> Fusion076089004005008002002002002003004002009002004002005004002028003
  Tool = -> Extrusion122
FEATURE [Part::Part2DObjectPython] Rectangle031  # Draft 2D object (typed FeaturePython)
  ChamferSize = 0
  Columns = 1
  FilletRadius = 0
  Height = 5
  Length = 1
  MakeFace = true
  Placement = pos=(105.704,-584.118,9) rot=(-0.707107,0.707107,0;3.14159rad)
  Rows = 1
FEATURE [Part::Extrusion] Extrusion123
  Base = -> Rectangle031
  Dir = (-2.1e-15,7e-16,3)
  DirMode = 0
  FaceMakerClass = Part::FaceMakerBullseye
  LengthFwd = 0
  LengthRev = 0
  Solid = true
  Symmetric = false
FEATURE [Part::Part2DObjectPython] Rectangle032  # Draft 2D object (typed FeaturePython)
  ChamferSize = 0
  Columns = 1
  FilletRadius = 0
  Height = 2
  Length = 3
  MakeFace = true
  Placement = pos=(100.704,-587.118,22) rot=(0.57735,0.57735,0.57735;2.0944rad)
  Rows = 1
  Support = -> [Extrusion120]
FEATURE [Part::Extrusion] Extrusion124
  Base = -> Rectangle032
  Dir = (5,0,0)
  DirMode = 0
  FaceMakerClass = Part::FaceMakerBullseye
  LengthFwd = 0
  LengthRev = 0
  Solid = true
  Symmetric = false
FEATURE [Part::Part2DObjectPython] Rectangle033  # Draft 2D object (typed FeaturePython)
  ChamferSize = 0
  Columns = 1
  FilletRadius = 0
  Height = 2
  Length = 5
  MakeFace = true
  Placement = pos=(135.704,-587.118,22) rot=(1,0,0;1.5708rad)
  Rows = 1
FEATURE [Part::Extrusion] Extrusion125
  Base = -> Rectangle033
  Dir = (0,3,-7e-16)
  DirMode = 0
  FaceMakerClass = Part::FaceMakerBullseye
  LengthFwd = 0
  LengthRev = 0
  Solid = true
  Symmetric = false
FEATURE [Part::MultiFuse] Fusion076089004005008002002002002003004002009002004002005004002028004
  Shapes = -> [Extrusion125,Cut279012006003037,Extrusion123,Extrusion124]
FEATURE [Part::MultiFuse] Fusion076089004005008002002002002003004002009002004002005004002028005
  Shapes = -> [Extrusion120,Fusion076089004005008002002002002003004002009002004002005004002028004]
FEATURE [Part::MultiFuse] Fusion076089004005008002002002002003004002009002004002005004002028006  label="FRAME"
  Shapes = -> [Fusion076089004005008002002002002003004002009002004002005004002028005,Cut279012006003027]
FEATURE [Part::Feature] Face061
  shape: bbox 9.957e-07 x 3 x 3 mm, 1 faces, 0 solids (baked)
FEATURE [Part::Extrusion] Extrusion126
  Base = -> Face061
  Dir = (-92.7,0,0)
  DirMode = 0
  FaceMakerClass = Part::FaceMakerBullseye
  LengthFwd = 0
  LengthRev = 0
  Solid = true
  Symmetric = false
FEATURE [Part::Part2DObjectPython] Rectangle034  # Draft 2D object (typed FeaturePython)
  ChamferSize = 0
  Columns = 1
  FilletRadius = 0
  Height = 3
  Length = 3
  MakeFace = true
  Placement = pos=(40.0036,-626.213,9.00025) rot=(1,0,0;1.5708rad)
  Rows = 1
FEATURE [Part::Extrusion] Extrusion127
  Base = -> Rectangle034
  Dir = (-1.06e-14,28,-1.896e-13)
  DirMode = 0
  FaceMakerClass = Part::FaceMakerBullseye
  LengthFwd = 0
  LengthRev = 0
  Solid = true
  Symmetric = false
FEATURE [Part::Part2DObjectPython] Circle021  # Draft 2D object (typed FeaturePython)
  FirstAngle = 0
  LastAngle = 0
  MakeFace = true
  Placement = pos=(40.0036,-626.213,12.0003) rot=(1,0,0;1.5708rad)
  Radius = 3
  Support = -> [Extrusion127]
FEATURE [Part::Extrusion] Extrusion128
  Base = -> Circle021
  Dir = (-1.06e-14,28,-1.896e-13)
  DirMode = 0
  FaceMakerClass = Part::FaceMakerBullseye
  LengthFwd = 0
  LengthRev = 0
  Solid = true
  Symmetric = false
FEATURE [Part::Cut] Cut279012006003038
  Base = -> Extrusion127
  Tool = -> Extrusion128
FEATURE [Part::Part2DObjectPython] Circle022  # Draft 2D object (typed FeaturePython)
  FirstAngle = 0
  LastAngle = 0
  MakeFace = true
  Placement = pos=(43.0036,-598.213,12.0003) rot=(0.57735,0.57735,0.57735;2.0944rad)
  Radius = 3
  Support = -> [Cut279012006003038]
FEATURE [Part::Extrusion] Extrusion129
  Base = -> Circle022
  Dir = (-3,4.26e-14,2.16e-14)
  DirMode = 0
  FaceMakerClass = Part::FaceMakerBullseye
  LengthFwd = 0
  LengthRev = 0
  Solid = true
  Symmetric = false
FEATURE [Part::Cut] Cut279012006003039
  Base = -> Cut279012006003038
  Tool = -> Extrusion129
FEATURE [Part::MultiFuse] Fusion076089004005008002002002002003004002009002004002005004002028007
  Shapes = -> [Cut279012006003039,Extrusion126]
FEATURE [Part::MultiFuse] Fusion076089004005008002002002002003004002009002004002005004002028008
  Shapes = -> [Fusion076089004005008002002002002003004002009002004002005004002028006,Fusion076089004005008002002002002003004002009002004002005004002027]
FEATURE [Part::MultiFuse] Fusion076089004005008002002002002003004002009002004002005004002028009
  Shapes = -> [Fusion076089004005008002002002002003004002009002004002005004002028007,Fusion076089004005008002002002002003004002009002004002005004002028008]
FEATURE [Part::Part2DObjectPython] Rectangle035  # Draft 2D object (typed FeaturePython)
  ChamferSize = 0
  Columns = 1
  FilletRadius = 0
  Height = 3
  Length = 30
  MakeFace = true
  Placement = pos=(105.704,-601.213,12.0003) rot=(0,0,1;0rad)
  Rows = 1
FEATURE [Part::Extrusion] Extrusion130
  Base = -> Rectangle035
  Dir = (0,0,-3.00025)
  DirMode = 0
  FaceMakerClass = Part::FaceMakerBullseye
  LengthFwd = 0
  LengthRev = 0
  Solid = true
  Symmetric = false
FEATURE [Part::Feature] Face062
  Placement = pos=(240.752,6.32824,0) rot=(0,0,1;0rad)
  shape: bbox 30 x 9.957e-07 x 15 mm, 1 faces, 0 solids (baked)
FEATURE [Part::Extrusion] Extrusion131
  Base = -> Face062
  Dir = (-1e-16,-0.0951993,-3.2e-15)
  DirMode = 0
  FaceMakerClass = Part::FaceMakerBullseye
  LengthFwd = 0
  LengthRev = 0
  Solid = true
  Symmetric = false
FEATURE [Part::Feature] Fusion004001_solid001  label="Connector"
  Placement = pos=(240.752,6.32824,0) rot=(0,0,1;0rad)
  shape: bbox 38 x 21 x 15 mm, 84 faces (baked)
FEATURE [Part::Fuse] Fusion076089004005008002002002002003004002009002004002005004002028012  label="Connector-Refined"
  Base = -> Fusion004001_solid001
  Tool = -> Extrusion131
FEATURE [Part::Cut] Cut279012006003040
  Base = -> Fusion076089004005008002002002002003004002009002004002005004002028009
  Tool = -> Extrusion130
FEATURE [Part::Part2DObjectPython] Rectangle036  # Draft 2D object (typed FeaturePython)
  ChamferSize = 0
  Columns = 1
  FilletRadius = 0
  Height = 25
  Length = 55
  MakeFace = true
  Placement = pos=(43.0036,-626.213,12.0003) rot=(0,0,1;0rad)
  Rows = 1
FEATURE [Part::Extrusion] Extrusion132
  Base = -> Rectangle036
  Dir = (0,0,-3.00025)
  DirMode = 0
  FaceMakerClass = Part::FaceMakerBullseye
  LengthFwd = 0
  LengthRev = 0
  Solid = true
  Symmetric = false
FEATURE [Part::Cut] Cut279012006003041
  Base = -> Cut279012006003040
  Tool = -> Extrusion132
FEATURE [Part::Part2DObjectPython] Rectangle037  # Draft 2D object (typed FeaturePython)
  ChamferSize = 0
  Columns = 1
  FilletRadius = 0
  Height = 26.2593
  Length = 57.2022
  MakeFace = true
  Placement = pos=(38.8014,-623.213,12.0003) rot=(0,0,1;0rad)
  Rows = 1
FEATURE [Part::Extrusion] Extrusion133
  Base = -> Rectangle037
  Dir = (0,0,-3.00025)
  DirMode = 0
  FaceMakerClass = Part::FaceMakerBullseye
  LengthFwd = 0
  LengthRev = 0
  Solid = true
  Symmetric = false
FEATURE [Part::Cut] Cut279012006003042  label="FRAME-Original"
  Base = -> Cut279012006003041
  Tool = -> Extrusion133
FEATURE [Part::Feature] Fusion076089004005008002002002002003004002009002004002005004002022001  label="Suppliers-Refined"
  shape: bbox 178.5 x 80 x 4 mm, 57 faces, 6 solids (baked)
FEATURE [Part::Feature] Cut279012006003042001  label="FRAME-Refined"
  shape: bbox 204 x 104 x 20.33 mm, 176 faces, 4 solids (baked)
FEATURE [Part::Feature] Face
  Placement = pos=(240.752,6.32824,0) rot=(0,0,1;0rad)
  shape: bbox 3 x 9.957e-07 x 7.5 mm, 1 faces, 0 solids (baked)
FEATURE [Part::Extrusion] Extrusion134
  Base = -> Face
  Dir = (0,-0.5,0)
  DirMode = 0
  FaceMakerClass = Part::FaceMakerBullseye
  LengthFwd = 0
  LengthRev = 0
  Solid = true
  Symmetric = false
FEATURE [Part::Cut] Cut279012006003042002
  Base = -> Fusion076089004005008002002002002003004002009002004002005004002028012
  Tool = -> Extrusion134
FEATURE [Part::Feature] Face063
  Placement = pos=(240.752,6.32824,0) rot=(0,0,1;0rad)
  shape: bbox 3 x 9.957e-07 x 7.5 mm, 1 faces, 0 solids (baked)
FEATURE [Part::Extrusion] Extrusion135
  Base = -> Face063
  Dir = (0,-0.5,0)
  DirMode = 0
  FaceMakerClass = Part::FaceMakerBullseye
  LengthFwd = 0
  LengthRev = 0
  Solid = true
  Symmetric = false
FEATURE [Part::Cut] Cut279012006003042003
  Base = -> Cut279012006003042002
  Tool = -> Extrusion135
FEATURE [Part::Feature] Face064
  Placement = pos=(240.752,6.32824,0) rot=(0,0,1;0rad)
  shape: bbox 4.959 x 8.04e-07 x 7 mm, 1 faces, 0 solids (baked)
FEATURE [Part::Extrusion] Extrusion136
  Base = -> Face064
  Dir = (2e-16,-0.5,8e-16)
  DirMode = 0
  FaceMakerClass = Part::FaceMakerBullseye
  LengthFwd = 0
  LengthRev = 0
  Solid = true
  Symmetric = false
FEATURE [Part::Feature] Face065
  Placement = pos=(240.752,6.32824,0) rot=(0,0,1;0rad)
  shape: bbox 5.083 x 1.002e-06 x 7 mm, 1 faces, 0 solids (baked)
FEATURE [Part::Extrusion] Extrusion137
  Base = -> Face065
  Dir = (8e-16,-0.5,0)
  DirMode = 0
  FaceMakerClass = Part::FaceMakerBullseye
  LengthFwd = 0
  LengthRev = 0
  Solid = true
  Symmetric = false
FEATURE [Part::MultiFuse] Fusion076089004005008002002002002003004002009002004002005004002028013
  Shapes = -> [Cut279012006003042003,Extrusion137]
FEATURE [Part::MultiFuse] Fusion076089004005008002002002002003004002009002004002005004002028014
  Shapes = -> [Extrusion136,Fusion076089004005008002002002002003004002009002004002005004002028013]
FEATURE [Part::Feature] Fusion076089004005008002002002002003004002009002004002005004002028014001  label="Fusion076089004005008002002002002003004002009002004002005004002028015"
  shape: bbox 38 x 21.1 x 15 mm, 83 faces (baked)
FEATURE [Part::Feature] Face067
  shape: bbox 8.04e-07 x 3 x 6 mm, 1 faces, 0 solids (baked)
FEATURE [Part::Extrusion] Extrusion138
  Base = -> Face067
  Dir = (1.00001,-1.6e-14,2.6e-15)
  DirMode = 0
  FaceMakerClass = Part::FaceMakerBullseye
  LengthFwd = 0
  LengthRev = 0
  Solid = true
  Symmetric = false
FEATURE [Part::MultiFuse] Fusion076089004005008002002002002003004002009002004002005004002028014002
  Shapes = -> [Fusion076089004005008002002002002003004002009002004002005004002028014001,Extrusion138]
FEATURE [Part::Feature] Face068
  shape: bbox 4.243e-07 x 3 x 6 mm, 1 faces, 0 solids (baked)
FEATURE [Part::Extrusion] Extrusion139
  Base = -> Face068
  Dir = (-0.999993,-1.03e-14,-6.1e-15)
  DirMode = 0
  FaceMakerClass = Part::FaceMakerBullseye
  LengthFwd = 0
  LengthRev = 0
  Solid = true
  Symmetric = false
FEATURE [Part::MultiFuse] Fusion076089004005008002002002002003004002009002004002005004002028014003
  Shapes = -> [Fusion076089004005008002002002002003004002009002004002005004002028014002,Extrusion139]
FEATURE [Part::Feature] Fusion076089004005008002002002002003004002009002004002005004002028014003001  label="Plugin-Refined"
  shape: bbox 38 x 21.1 x 15 mm, 83 faces (baked)
FEATURE [Part::Part2DObjectPython] Line  # Draft 2D object (typed FeaturePython)
  ChamferSize = 0
  Closed = false
  End = (97.0036,-626.313,12.0003)
  FilletRadius = 0
  Length = 0.1
  MakeFace = true
  Placement = pos=(97.0036,-626.213,12.0003) rot=(0,0,1;0rad)
  Points = (2) [(0,0,0),(0,-0.1,0)]
  Start = (97.0036,-626.213,12.0003)
  Subdivisions = 0
  Support = -> [Cut279012006003042001]
FEATURE [Part::Feature] Face069
  shape: bbox 2.001 x 0.001324 x 3.001 mm, 1 faces, 0 solids (baked)
FEATURE [Part::Extrusion] Extrusion140
  Base = -> Face069
  Dir = (0,-0.1,0)
  DirMode = 0
  FaceMakerClass = Part::FaceMakerBullseye
  LengthFwd = 0
  LengthRev = 0
  Solid = true
  Symmetric = false
FEATURE [Part::Cut] Cut279012006003042004
  Base = -> Cut279012006003042
  Tool = -> Extrusion140
FEATURE [Part::Feature] Face070
  shape: bbox 1.136e-06 x 2 x 3 mm, 1 faces, 0 solids (baked)
FEATURE [Part::Extrusion] Extrusion141
  Base = -> Face070
  Dir = (0.1,0,0)
  DirMode = 0
  FaceMakerClass = Part::FaceMakerBullseye
  LengthFwd = 0
  LengthRev = 0
  Solid = true
  Symmetric = false
FEATURE [Part::Cut] Cut279012006003042005  label="FRAME-Without Refine"
  Base = -> Cut279012006003042004
  Tool = -> Extrusion141
FEATURE [Part::Part2DObjectPython] Circle  # Draft 2D object (typed FeaturePython)
  FirstAngle = 0
  LastAngle = 0
  MakeFace = true
  Placement = pos=(167.204,-605.12,13) rot=(0,0,1;0rad)
  Radius = 1.3
FEATURE [Part::Extrusion] Extrusion142
  Base = -> Circle
  Dir = (0,0,-4)
  DirMode = 0
  FaceMakerClass = Part::FaceMakerBullseye
  LengthFwd = 0
  LengthRev = 0
  Solid = true
  Symmetric = false
FEATURE [Part::Part2DObjectPython] Rectangle038  # Draft 2D object (typed FeaturePython)
  ChamferSize = 0
  Columns = 1
  FilletRadius = 0
  Height = 6.60049
  Length = 6.41038
  MakeFace = true
  Placement = pos=(163.949,-630.72,13) rot=(0,0,1;0rad)
  Rows = 1
FEATURE [Part::Part2DObjectPython] Circle023  # Draft 2D object (typed FeaturePython)
  FirstAngle = 0
  LastAngle = 0
  MakeFace = true
  Placement = pos=(167.204,-628.12,13) rot=(0,0,1;0rad)
  Radius = 1.3
FEATURE [Part::Part2DObjectPython] Rectangle039  # Draft 2D object (typed FeaturePython)
  ChamferSize = 0
  Columns = 1
  FilletRadius = 0
  Height = 6.60049
  Length = 6.41038
  MakeFace = true
  Placement = pos=(163.949,-607.72,13) rot=(0,0,1;0rad)
  Rows = 1
FEATURE [Part::Extrusion] Extrusion143
  Base = -> Rectangle039
  Dir = (0,0,-4)
  DirMode = 0
  FaceMakerClass = Part::FaceMakerBullseye
  LengthFwd = 0
  LengthRev = 0
  Solid = true
  Symmetric = false
FEATURE [Part::Extrusion] Extrusion144
  Base = -> Circle023
  Dir = (0,0,-4)
  DirMode = 0
  FaceMakerClass = Part::FaceMakerBullseye
  LengthFwd = 0
  LengthRev = 0
  Solid = true
  Symmetric = false
FEATURE [Part::Extrusion] Extrusion145
  Base = -> Rectangle038
  Dir = (0,0,-4)
  DirMode = 0
  FaceMakerClass = Part::FaceMakerBullseye
  LengthFwd = 0
  LengthRev = 0
  Solid = true
  Symmetric = false
FEATURE [Part::Part2DObjectPython] Rectangle040  # Draft 2D object (typed FeaturePython)
  ChamferSize = 0
  Columns = 1
  FilletRadius = 0
  Height = 6.41038
  Length = 16.3995
  MakeFace = true
  Placement = pos=(163.949,-624.12,9) rot=(0.707107,0.707107,0;3.14159rad)
  Rows = 1
  Support = -> [Extrusion143]
FEATURE [Part::Cut] Cut279012006003042006
  Base = -> Extrusion143
  Tool = -> Extrusion142
FEATURE [Part::Cut] Cut279012006003042007
  Base = -> Extrusion145
  Tool = -> Extrusion144
FEATURE [Part::Extrusion] Extrusion146
  Base = -> Rectangle040
  Dir = (0,0,1.6)
  DirMode = 0
  FaceMakerClass = Part::FaceMakerBullseye
  LengthFwd = 0
  LengthRev = 0
  Solid = true
  Symmetric = false
FEATURE [Part::MultiFuse] Fusion076089004005008002002002002003004002009002004002005004002028014003002
  Shapes = -> [Extrusion146,Cut279012006003042006,Cut279012006003042007]
FEATURE [Part::MultiFuse] Fusion076089004005008002002002002003004002009002004002005004002028014003003  label="SUPPLY"
  Shapes = -> [Fusion076089004005008002002002002003004002009002004002005004002028014003002,Fusion076089004005008002002002002003004002009002004002005004002022001]
FEATURE [Part::Feature] Face071
  shape: bbox 7.839e-07 x 3 x 3 mm, 1 faces, 0 solids (baked)
FEATURE [Part::Extrusion] Extrusion147
  Base = -> Face071
  Dir = (-21.3,-8.1e-15,-6e-16)
  DirMode = 0
  FaceMakerClass = Part::FaceMakerBullseye
  LengthFwd = 0
  LengthRev = 0
  Solid = true
  Symmetric = false
FEATURE [Part::MultiFuse] Fusion076089004005008002002002002003004002009002004002005004002028014003004  label="FRAME001"
  Shapes = -> [Cut279012006003042005,Extrusion147]
FEATURE [Part::MultiFuse] Fusion076089004005008002002002002003004002009002004002005004002028014003005  label="LAMP.BASE"
  Shapes = -> [Fusion076089004005008002002002002003004002009002004002005004002028014003003,Fusion076089004005008002002002002003004002009002004002005004002028014003004,Fusion076089004005008002002002002003004002009002004002005004002028014003001]
